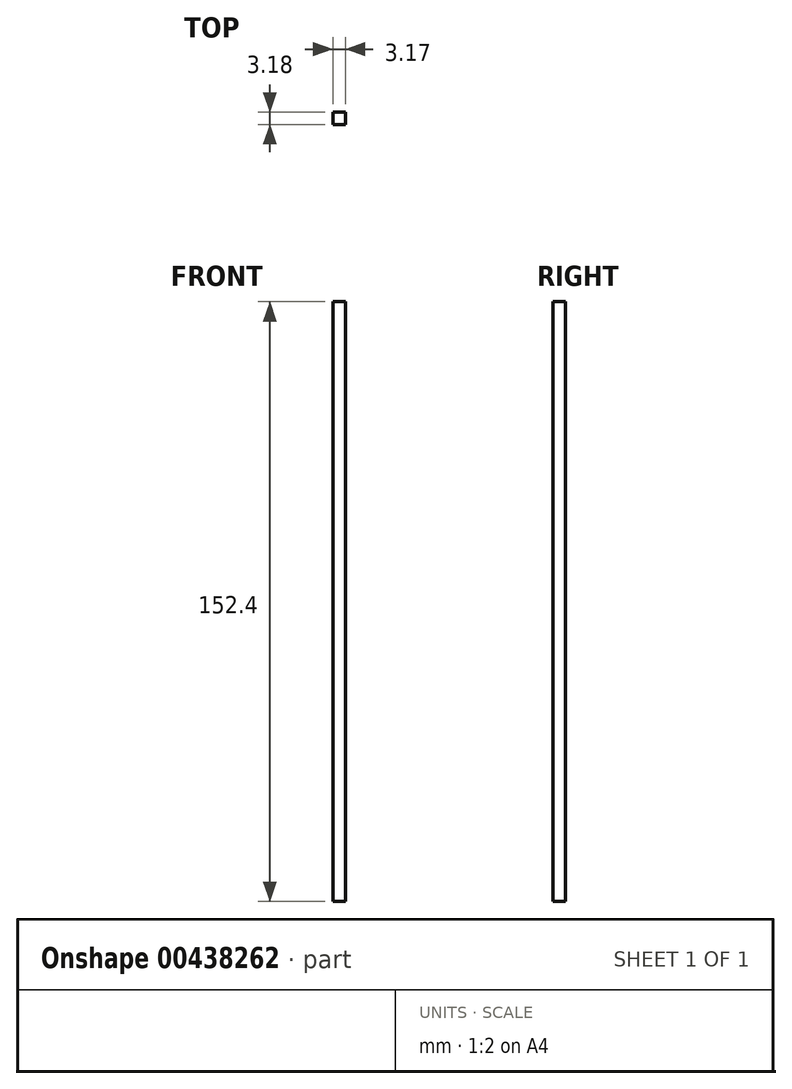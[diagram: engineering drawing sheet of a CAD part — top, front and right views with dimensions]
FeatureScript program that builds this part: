
annotation { "Feature Type Name" : "Feature", "Feature Type Description" : "" }
export const myFeature = defineFeature(function(context is Context, id is Id, definition is map)
    precondition{}
    {
        {
            var Q0;
            Q0=qCreatedBy(makeId("Top.planeOp"),FACE);
            var sketch = newSketch(context, id + "F0", { "sketchPlane" : qUnion([Q0])});
            skLineSegment(sketch, "E0.bottom", {"start": v(-44.17, 33.15) * mm, "end": v(-41, 33.15) * mm});
            skLineSegment(sketch, "E0.top", {"start": v(-44.17, 29.97) * mm, "end": v(-41, 29.97) * mm});
            skLineSegment(sketch, "E0.left", {"start": v(-44.17, 33.15) * mm, "end": v(-44.17, 29.97) * mm});
            skLineSegment(sketch, "E0.right", {"start": v(-41, 33.15) * mm, "end": v(-41, 29.97) * mm});
            skSolve(sketch);
        }
        {
            var Q0;
            Q0 = qSketchRegion(id + "F0", true);
            extrude(context, id + "F1", {"entities" : qUnion([Q0]), "depth" : 152.4 * mm});
        }
    });
